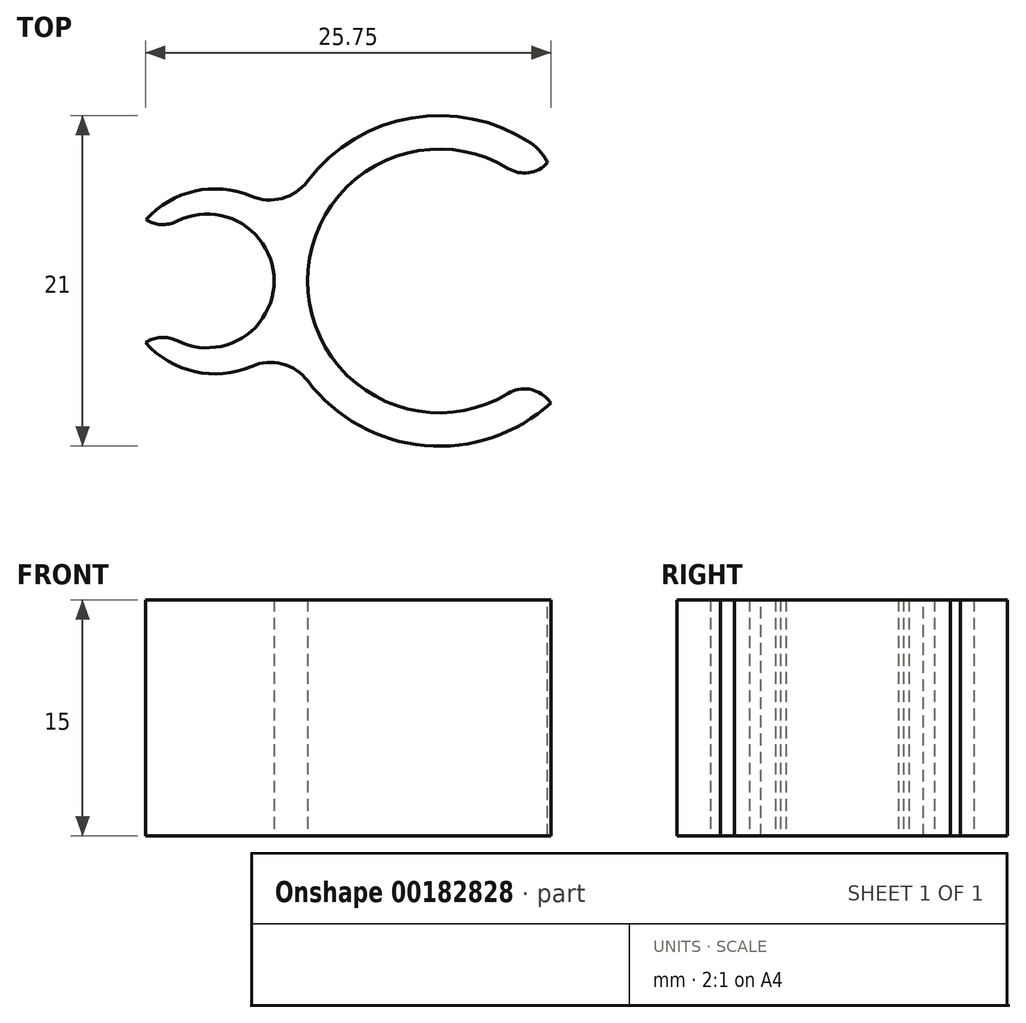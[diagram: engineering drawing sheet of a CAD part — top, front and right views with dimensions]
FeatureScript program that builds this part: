
annotation { "Feature Type Name" : "Feature", "Feature Type Description" : "" }
export const myFeature = defineFeature(function(context is Context, id is Id, definition is map)
    precondition{}
    {
        {
            var Q0;
            Q0=qCreatedBy(makeId("Top.planeOp"),FACE);
            var sketch = newSketch(context, id + "F0", { "sketchPlane" : qUnion([Q0])});
            skLineSegment(sketch, "E0", {"start": v(5.66, 6.17) * mm, "end": v(7.1, 7.74) * mm});
            skLineSegment(sketch, "E1", {"start": v(5.66, -6.17) * mm, "end": v(7.1, -7.74) * mm});
            skArc(sketch, "E2", {"start": v(5.66, 6.17) * mm, "mid": v(-8.38, 0) * mm, "end": v(5.66, -6.17) * mm});
            skArc(sketch, "E3", {"start": v(7.1, 7.74) * mm, "mid": v(-4.16, 9.64) * mm, "end": v(-10.5, 0.15) * mm});
            skArc(sketch, "E4", {"start": v(-18.66, -3.91) * mm, "mid": v(-8.38, -0.04) * mm, "end": v(-18.63, 3.89) * mm});
            skArc(sketch, "E5", {"start": v(-17.75, -3) * mm, "mid": v(-10.5, 0) * mm, "end": v(-17.75, 3) * mm});
            skArc(sketch, "E6", {"start": v(-10.5, -0.15) * mm, "mid": v(-4.16, -9.64) * mm, "end": v(7.1, -7.74) * mm});
            skLineSegment(sketch, "E7", {"start": v(-17.75, 3) * mm, "end": v(-18.7, 3.95) * mm});
            skLineSegment(sketch, "E8", {"start": v(-17.75, -3) * mm, "end": v(-18.66, -3.91) * mm});
            skSolve(sketch);
        }
        {
            var Q0;
            Q0=qSketchRegion(id+"F0",true);
            extrude(context, id + "F1", {"entities" : qUnion([Q0]), "depth" : 15 * mm});
        }
        {
            var Q0;
            Q0=makeQuery(id+"F1.opExtrude","SWEPT_EDGE",EDGE,{"disambiguationData":[OSD([sQuery(id+"F0.wireOp",EDGE,"E0"),sQuery(id+"F0.wireOp",EDGE,"E2")])]});
            var Q1;
            Q1=makeQuery(id+"F1.opExtrude","SWEPT_EDGE",EDGE,{"disambiguationData":[OSD([sQuery(id+"F0.wireOp",EDGE,"E1"),sQuery(id+"F0.wireOp",EDGE,"E2")])]});
            fillet(context, id + "F2", {"entities" : qUnion([Q0, Q1]), "radius" : 2 * mm, "tangentPropagation" : true, "allowEdgeOverflow" : false});
        }
        {
            var Q0;
            {var subQ0=sQuery(id+"F0.wireOp",EDGE,"E3");var subQ1=sQuery(id+"F0.wireOp",EDGE,"ZSCY8b5y-4nQt-1SJT-bSQS-RtF6pSp449vb");Q0=makeQuery(id+"F1.opExtrude","SWEPT_EDGE",EDGE,{"disambiguationData":[OSD([subQ1,subQ0]),TDD([makeQuery(id+"F0.imprint","INTERSECT",VERTEX,{"disambiguationData":[OD(0.0)],"derivedFrom":[subQ1,subQ0]})])]});}
            var Q1;
            {var subQ0=sQuery(id+"F0.wireOp",EDGE,"E3");var subQ1=sQuery(id+"F0.wireOp",EDGE,"ZSCY8b5y-4nQt-1SJT-bSQS-RtF6pSp449vb");Q1=makeQuery(id+"F1.opExtrude","SWEPT_EDGE",EDGE,{"disambiguationData":[OSD([subQ1,subQ0]),TDD([makeQuery(id+"F0.imprint","INTERSECT",VERTEX,{"disambiguationData":[OD(1.0)],"derivedFrom":[subQ1,subQ0]})])]});}
            var Q2;
            Q2=makeQuery(id+"F1.opExtrude","SWEPT_EDGE",EDGE,{"disambiguationData":[OSD([sQuery(id+"F0.wireOp",EDGE,"E4"),sQuery(id+"F0.wireOp",EDGE,"E6")])]});
            fillet(context, id + "F3", {"entities" : qUnion([Q0, Q1, Q2]), "radius" : 3 * mm, "tangentPropagation" : true, "allowEdgeOverflow" : false});
        }
        {
            var Q0;
            Q0=makeQuery(id+"F1.opExtrude","SWEPT_EDGE",EDGE,{"disambiguationData":[OSD([sQuery(id+"F0.wireOp",EDGE,"rEuPobd8-yjFE-shQi-krWZ-2xlXbWUtzDBs"),sQuery(id+"F0.wireOp",EDGE,"E5")])]});
            var Q1;
            Q1=makeQuery(id+"F1.opExtrude","SWEPT_EDGE",EDGE,{"disambiguationData":[OSD([sQuery(id+"F0.wireOp",EDGE,"3cLjUToE-DPJw-2F6M-vbHq-9WFNUtiZbH4s"),sQuery(id+"F0.wireOp",EDGE,"E5")])]});
            fillet(context, id + "F4", {"entities" : qUnion([Q0, Q1]), "radius" : 2 * mm, "tangentPropagation" : true, "allowEdgeOverflow" : false});
        }
    });
